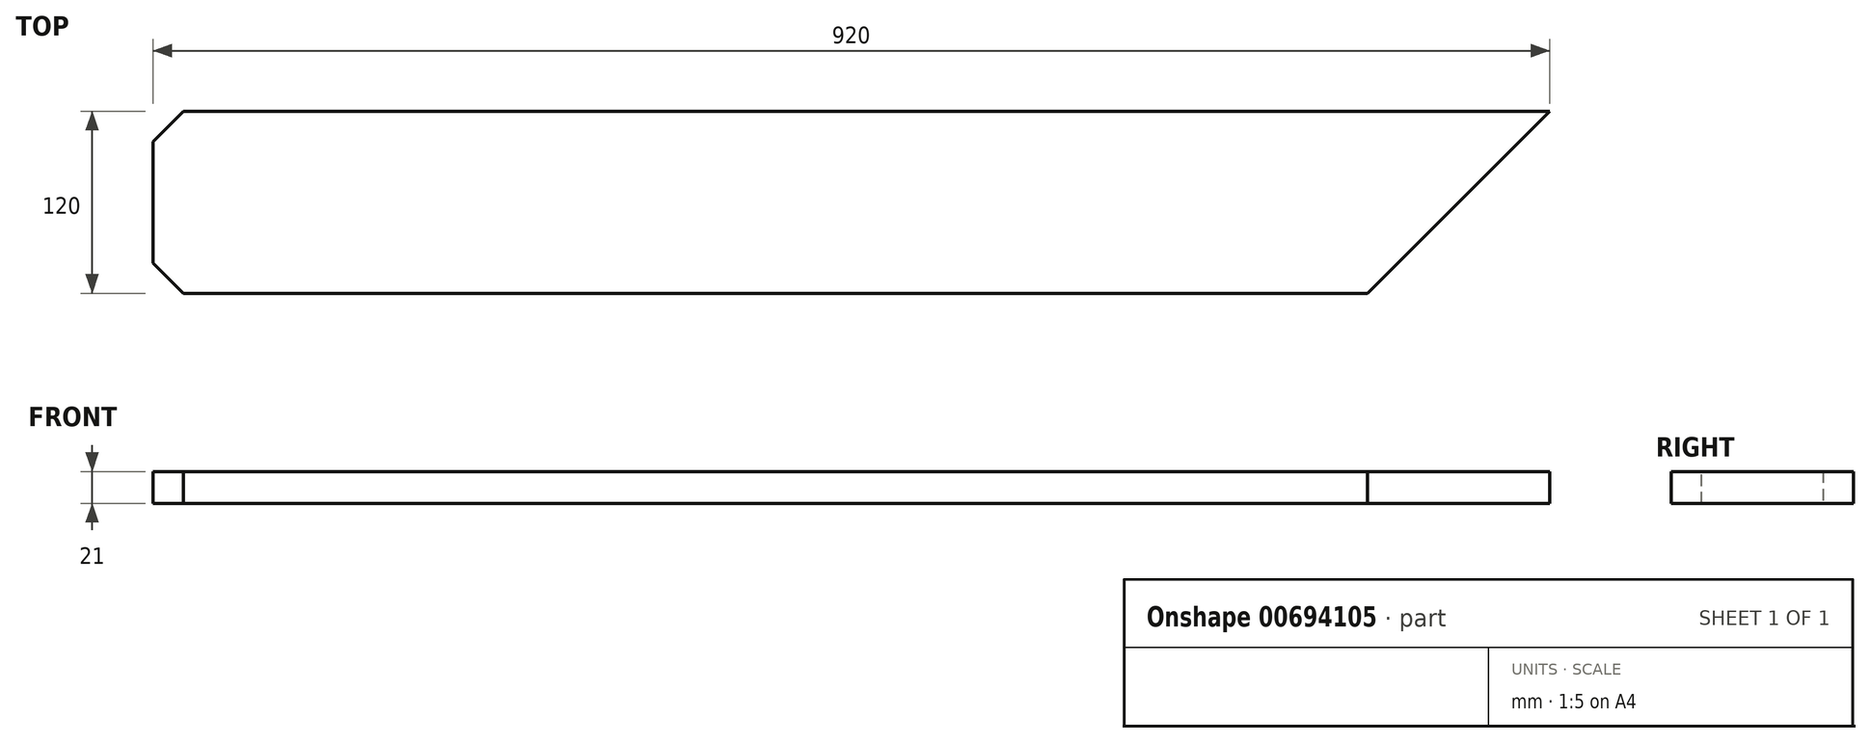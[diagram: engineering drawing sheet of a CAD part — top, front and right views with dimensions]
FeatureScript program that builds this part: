
annotation { "Feature Type Name" : "Feature", "Feature Type Description" : "" }
export const myFeature = defineFeature(function(context is Context, id is Id, definition is map)
    precondition{}
    {
        {
            var Q0;
            Q0=qCreatedBy(makeId("Top.planeOp"),FACE);
            var sketch = newSketch(context, id + "F0", { "sketchPlane" : qUnion([Q0])});
            skLineSegment(sketch, "E0.bottom", {"start": v(-460, -60) * mm, "end": v(460, -60) * mm});
            skLineSegment(sketch, "E0.top", {"start": v(-460, 60) * mm, "end": v(460, 60) * mm});
            skLineSegment(sketch, "E0.left", {"start": v(-460, -60) * mm, "end": v(-460, 60) * mm});
            skLineSegment(sketch, "E0.right", {"start": v(460, -60) * mm, "end": v(460, 60) * mm});
            skSolve(sketch);
        }
        {
            var Q0;
            Q0=makeQuery(id+"F0.imprint","IMPRINT",FACE,{"disambiguationData":[TD([[makeQuery(id+"F0.imprint","IMPRINT",EDGE,{"derivedFrom":sQuery(id+"F0.wireOp",EDGE,"E0.bottom")}),1.0]])]});
            extrude(context, id + "F1", {"entities" : qUnion([Q0]), "depth" : 21 * mm, "offsetDistance" : 25 * mm});
        }
        {
            var Q0;
            Q0=makeQuery(id+"F1.opExtrude","SWEPT_EDGE",EDGE,{"disambiguationData":[OSD([sQuery(id+"F0.wireOp",EDGE,"E0.top"),sQuery(id+"F0.wireOp",EDGE,"E0.left")])]});
            var Q1;
            Q1=makeQuery(id+"F1.opExtrude","SWEPT_EDGE",EDGE,{"disambiguationData":[OSD([sQuery(id+"F0.wireOp",EDGE,"E0.bottom"),sQuery(id+"F0.wireOp",EDGE,"E0.left")])]});
            chamfer(context, id + "F2", {"entities" : qUnion([Q0, Q1]), "width" : 20 * mm, "tangentPropagation" : true});
        }
        {
            var Q0;
            Q0=makeQuery(id+"F1.opExtrude","SWEPT_EDGE",EDGE,{"disambiguationData":[OSD([sQuery(id+"F0.wireOp",EDGE,"E0.bottom"),sQuery(id+"F0.wireOp",EDGE,"E0.right")])]});
            chamfer(context, id + "F3", {"entities" : qUnion([Q0]), "width" : 120 * mm, "tangentPropagation" : true});
        }
    });
